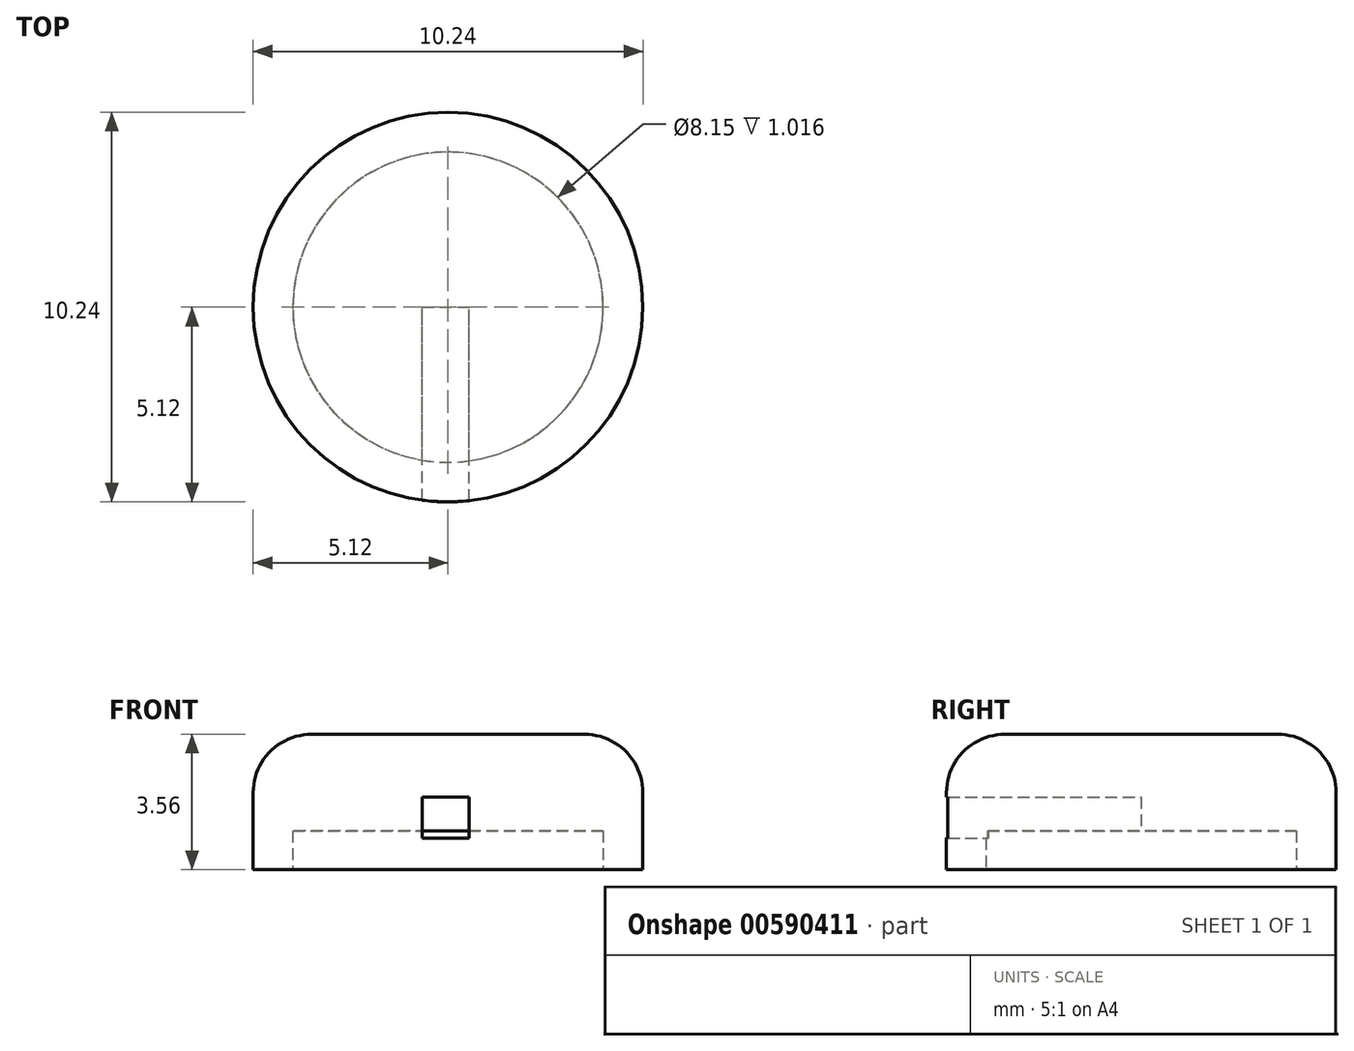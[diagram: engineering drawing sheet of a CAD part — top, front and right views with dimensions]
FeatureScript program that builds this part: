
annotation { "Feature Type Name" : "Feature", "Feature Type Description" : "" }
export const myFeature = defineFeature(function(context is Context, id is Id, definition is map)
    precondition{}
    {
        {
            var Q0;
            Q0=qCreatedBy(makeId("Top.planeOp"),FACE);
            var sketch = newSketch(context, id + "F0", { "sketchPlane" : qUnion([Q0])});
            skCircle(sketch, "E0", {"center": v(0, 0) * mm, "radius": 5.12 * mm});
            skSolve(sketch);
        }
        {
            var Q0;
            Q0=makeQuery(id+"F0.imprint","IMPRINT",FACE,{"disambiguationData":[TD([[makeQuery(id+"F0.imprint","IMPRINT",EDGE,{"derivedFrom":sQuery(id+"F0.wireOp",EDGE,"E0")}),1.0]])]});
            var Q1;
            Q1=sQuery(id+"F0.wireOp",EDGE,"E0");
            extrude(context, id + "F1", {"entities" : qUnion([Q0]), "surfaceEntities" : qUnion([Q1]), "depth" : 3.56 * mm, "offsetDistance" : 25.4 * mm});
        }
        {
            var Q0;
            Q0=qCreatedBy(makeId("Top.planeOp"),FACE);
            var sketch = newSketch(context, id + "F2", { "sketchPlane" : qUnion([Q0])});
            skCircle(sketch, "E1", {"center": v(0, 0) * mm, "radius": 4.08 * mm});
            skSolve(sketch);
        }
        {
            var Q0;
            Q0=makeQuery(id+"F2.imprint","IMPRINT",FACE,{"disambiguationData":[TD([[makeQuery(id+"F2.imprint","IMPRINT",EDGE,{"derivedFrom":sQuery(id+"F2.wireOp",EDGE,"E1")}),1.0]])]});
            var Q1;
            Q1=sQuery(id+"F2.wireOp",EDGE,"E1");
            extrude(context, id + "F3", {"entities" : qUnion([Q0]), "operationType" : NewBodyOperationType.REMOVE, "surfaceEntities" : qUnion([Q1]), "depth" : 1.02 * mm, "offsetDistance" : 25.4 * mm});
        }
        {
            var Q0;
            Q0=makeQuery(id+"F1.opExtrude","CAP_EDGE",EDGE,{"disambiguationData":[OSD([sQuery(id+"F0.wireOp",EDGE,"E0")])],"isStart":false});
            fillet(context, id + "F4", {"entities" : qUnion([Q0]), "radius" : 1.53 * mm, "tangentPropagation" : true, "allowEdgeOverflow" : false});
        }
        {
            var Q0;
            Q0=qCreatedBy(makeId("Front.planeOp"),FACE);
            var sketch = newSketch(context, id + "F5", { "sketchPlane" : qUnion([Q0])});
            skLineSegment(sketch, "E2.bottom", {"start": v(-0.67, 1.9) * mm, "end": v(0.55, 1.9) * mm});
            skLineSegment(sketch, "E2.top", {"start": v(-0.67, 0.83) * mm, "end": v(0.55, 0.83) * mm});
            skLineSegment(sketch, "E2.left", {"start": v(-0.67, 1.9) * mm, "end": v(-0.67, 0.83) * mm});
            skLineSegment(sketch, "E2.right", {"start": v(0.55, 1.9) * mm, "end": v(0.55, 0.83) * mm});
            skSolve(sketch);
        }
        {
            var Q0;
            Q0 = qSketchRegion(id + "F5", true);
            extrude(context, id + "F6", {"entities" : qUnion([Q0]), "operationType" : NewBodyOperationType.REMOVE, "depth" : 5.5 * mm, "offsetDistance" : 25.4 * mm});
        }
    });
